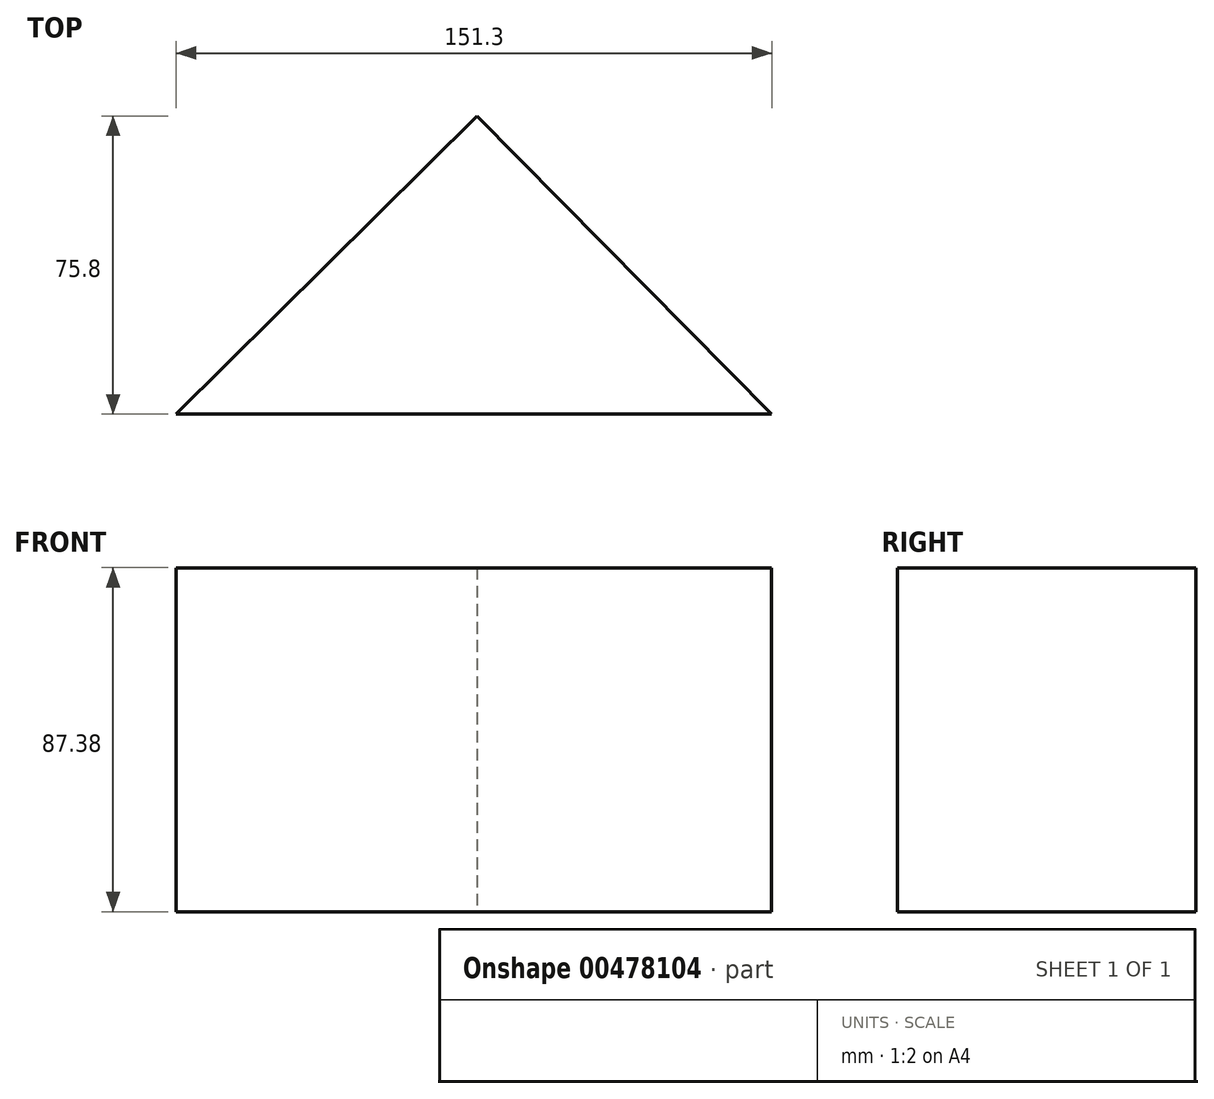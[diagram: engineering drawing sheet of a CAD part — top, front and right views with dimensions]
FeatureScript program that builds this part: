
annotation { "Feature Type Name" : "Feature", "Feature Type Description" : "" }
export const myFeature = defineFeature(function(context is Context, id is Id, definition is map)
    precondition{}
    {
        {
            var Q0;
            Q0=qCreatedBy(makeId("Top.planeOp"),FACE);
            var sketch = newSketch(context, id + "F0", { "sketchPlane" : qUnion([Q0])});
            skLineSegment(sketch, "E0", {"start": v(0, 75.8) * mm, "end": v(-76.4, 0) * mm});
            skLineSegment(sketch, "E1", {"start": v(-76.4, 0) * mm, "end": v(74.9, 0) * mm});
            skLineSegment(sketch, "E2", {"start": v(74.9, 0) * mm, "end": v(0, 75.8) * mm});
            skSolve(sketch);
        }
        {
            var Q0;
            Q0 = qSketchRegion(id + "F0", true);
            extrude(context, id + "F1", {"entities" : qUnion([Q0]), "depth" : 87.38 * mm});
        }
    });
